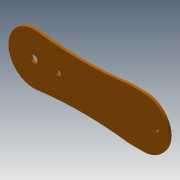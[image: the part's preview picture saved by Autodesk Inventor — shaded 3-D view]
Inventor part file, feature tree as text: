
AUTODESK INVENTOR PART (.ipt)
format: ipt  version: 2013 (Build 170138000, 138)  size: 136,704 bytes
history: native  units: mm
features: extrude x4, sketch x4
ambient origin geometry x8: Origin, YZ Plane, XZ Plane, XY Plane, X Axis, Y Axis, Z Axis, Center Point
bodies: Solid1 (feature_tree)
feature tree (8):
  extrude  "Extrusion1"  Depth=40.2mm
  extrude  "Extrusion2"  Depth=20.0mm
  extrude  "Extrusion3"  Depth=6.0mm
  extrude  "Extrusion4"  Depth=10.0mm
  sketch  "Sketch1"  dims[d2=42.0mm d11=40.2mm]
  sketch  "Sketch2"  dims[d13=55.0mm d14=20.0mm]
  sketch  "Sketch3"  dims[d23=3.0mm d24=6.0mm]
  sketch  "Sketch4"  dims[d25=40.0mm d26=10.0mm d27=3.0mm d28=40.0mm d29=4.0mm d30=2.0mm d31=0.0mm d32=2.0mm d33=0.0mm d34=20.0mm d35=4.0mm d36=2.0mm d37=0.0mm d38=2.0mm d39=0.0mm]
